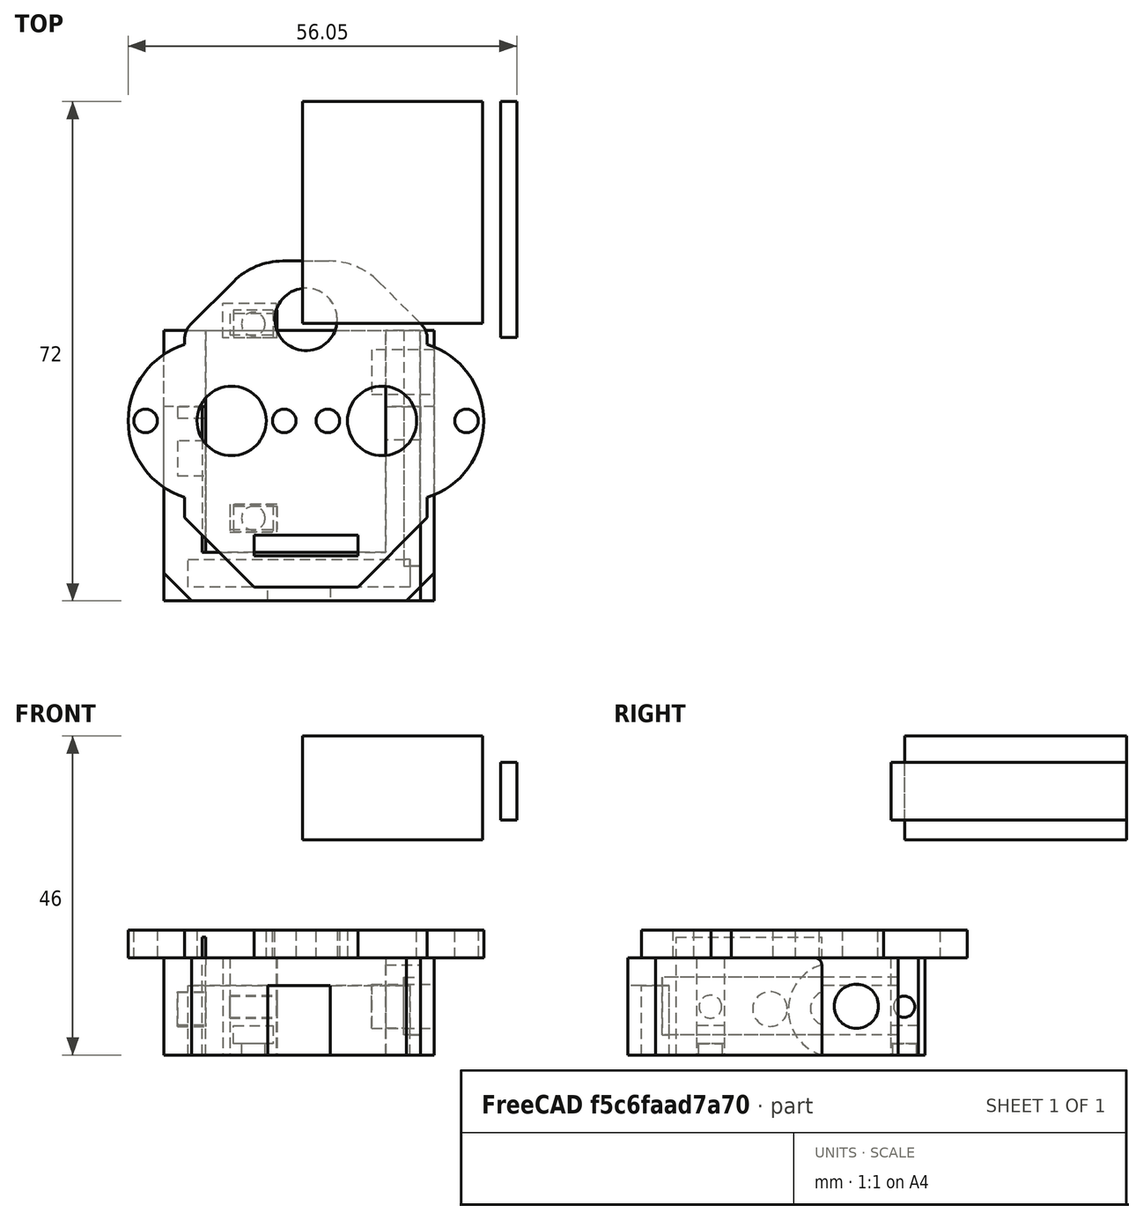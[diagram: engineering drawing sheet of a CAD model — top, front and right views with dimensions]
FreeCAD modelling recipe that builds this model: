
FCSTD DOCUMENT  (FreeCAD 0.14R2935 (Git))
Label: cuello3
License: CC-BY 3.0
LicenseURL: http://creativecommons.org/licenses/by/3.0/
objects: Sketcher::SketchObject×9, PartDesign::Pocket×8, Part::Feature×3, Part::Box×3, PartDesign::Fillet×3, PartDesign::Chamfer×2, Mesh::Feature×1, PartDesign::Pad×1, Part::MultiFuse×1, Part::Cut×1
note: 40 computed .brp shape members not serialized (recipe doc carries the construction recipe); baked Part::Feature solids carry a one-line shape summary decoded from their .brp

FEATURE [Part::Feature] Pad  label="Pad008"
  shape: bbox 51.29 x 47 x 18 mm, 56 faces (baked)
FEATURE [Mesh::Feature] _g_servo  label="9g_servo"
  Placement = pos=(3,-10,-24) rot=(0.57735,0.57735,0.57735;2.0944rad)
FEATURE [Part::Box] Box
  Height = 14
  Length = 37
  Placement = pos=(-14,-33,-31) rot=(0,0,1;0rad)
  Width = 39
FEATURE [Sketcher::SketchObject] Sketch
  ExternalGeometry = -> [Box]
  Placement = pos=(-14,-33,-31) rot=(1,0,0;3.14159rad)
  Support = -> Box [Face5]
  sketch-geometry (4):
    g0: LineSegment StartX=32 StartY=-39 StartZ=0 EndX=6 EndY=-39 EndZ=0
    g1: LineSegment StartX=6 StartY=-39 StartZ=0 EndX=6 EndY=-7 EndZ=0
    g2: LineSegment StartX=6 StartY=-7 StartZ=0 EndX=32 EndY=-7 EndZ=0
    g3: LineSegment StartX=32 StartY=-7 StartZ=0 EndX=32 EndY=-39 EndZ=0
  constraints (12):
    c: Coincident(g0,g1)
    c: Coincident(g1,g2)
    c: Coincident(g2,g3)
    c: Coincident(g3,g0)
    c: Horizontal(g0)
    c: Horizontal(g2)
    c: Vertical(g1)
    c: Vertical(g3)
    c: PointOnObject(g0,g-3)
    c: DistanceX(g-2,g1) = 6
    c: Distance(g2,g-4) = 5
    c: DistanceY(g-1,g2) = -7
FEATURE [PartDesign::Pocket] Pocket
  Length = 15
  Placement = pos=(-14,-33,-31) rot=(0,0,1;0rad)
  Sketch = -> Sketch
  Type = 0
FEATURE [Sketcher::SketchObject] Sketch001
  ExternalGeometry = -> [Pocket]
  Placement = pos=(-14,6,-31) rot=(0,0.707107,0.707107;3.14159rad)
  Support = -> Pocket [Face10]
  sketch-geometry (4):
    g0: LineSegment StartX=-36.9 StartY=11.215 StartZ=0 EndX=-34.6 EndY=11.215 EndZ=0
    g1: LineSegment StartX=-34.6 StartY=11.215 StartZ=0 EndX=-34.6 EndY=2.91495 EndZ=0
    g2: LineSegment StartX=-34.6 StartY=2.91495 StartZ=0 EndX=-36.9 EndY=2.91495 EndZ=0
    g3: LineSegment StartX=-36.9 StartY=2.91495 StartZ=0 EndX=-36.9 EndY=11.215 EndZ=0
  constraints (11):
    c: Coincident(g0,g1)
    c: Coincident(g1,g2)
    c: Coincident(g2,g3)
    c: Coincident(g3,g0)
    c: Horizontal(g0)
    c: Horizontal(g2)
    c: Vertical(g1)
    c: Vertical(g3)
    c: DistanceX(g2) = -2.3
    c: DistanceY(g3) = 8.3
    c: Distance(g0,g-3) = 2.6
FEATURE [PartDesign::Pocket] Pocket001
  Length = 34
  Placement = pos=(-14,-33,-31) rot=(0,0,1;0rad)
  Sketch = -> Sketch001
  Type = 0
FEATURE [Sketcher::SketchObject] Sketch002
  ExternalGeometry = -> [Pocket001]
  Placement = pos=(23,-33,-31) rot=(0.57735,0.57735,0.57735;2.0944rad)
  Support = -> Pocket001 [Face6]
  sketch-geometry (4):
    g0: LineSegment StartX=0 StartY=14 StartZ=0 EndX=39 EndY=14 EndZ=0
    g1: LineSegment StartX=39 StartY=14 StartZ=0 EndX=39 EndY=0 EndZ=0
    g2: LineSegment StartX=39 StartY=0 StartZ=0 EndX=0 EndY=0 EndZ=0
    g3: LineSegment StartX=0 StartY=0 StartZ=0 EndX=0 EndY=14 EndZ=0
  constraints (11):
    c: Coincident(g0,g1)
    c: Coincident(g1,g2)
    c: Coincident(g2,g3)
    c: Coincident(g3,g0)
    c: Horizontal(g0)
    c: Horizontal(g2)
    c: Vertical(g1)
    c: Vertical(g3)
    c: Coincident(g1,g-4)
    c: Coincident(g0,g-4)
    c: Coincident(g0,g-3)
FEATURE [PartDesign::Pad] Pad001
  Length = 2
  Length2 = 100
  Placement = pos=(-14,-33,-31) rot=(0,0,1;0rad)
  Sketch = -> Sketch002
  Type = 0
FEATURE [Part::Feature] Pad002  label="Pad009"
  shape: bbox 39 x 39 x 14 mm, 15 faces (baked)
FEATURE [Sketcher::SketchObject] Sketch003
  Placement = pos=(25,0,0) rot=(0.57735,0.57735,0.57735;2.0944rad)
  Support = -> Pad002 [Face1]
  sketch-geometry (1):
    g0: Circle CenterX=0 CenterY=-23.9671 CenterZ=0 NormalX=0 NormalY=0 NormalZ=1 Radius=3.18985
  constraints (1):
    c: PointOnObject(g0,g-2)
FEATURE [PartDesign::Pocket] Pocket002
  Length = 9
  Sketch = -> Sketch003
  Type = 0
FEATURE [Sketcher::SketchObject] Sketch004
  ExternalGeometry = -> [Pocket002]
  Placement = pos=(0,6,0) rot=(0,0.707107,0.707107;3.14159rad)
  Support = -> Pocket002 [Face4]
  sketch-geometry (4):
    g0: LineSegment StartX=-20.6 StartY=-21.0207 StartZ=0 EndX=-18 EndY=-21.0207 EndZ=0
    g1: LineSegment StartX=-18 StartY=-21.0207 StartZ=0 EndX=-18 EndY=-27.0975 EndZ=0
    g2: LineSegment StartX=-18 StartY=-27.0975 StartZ=0 EndX=-20.6 EndY=-27.0975 EndZ=0
    g3: LineSegment StartX=-20.6 StartY=-27.0975 StartZ=0 EndX=-20.6 EndY=-21.0207 EndZ=0
  constraints (10):
    c: Coincident(g0,g1)
    c: Coincident(g1,g2)
    c: Coincident(g2,g3)
    c: Coincident(g3,g0)
    c: Horizontal(g0)
    c: Horizontal(g2)
    c: Vertical(g1)
    c: Vertical(g3)
    c: PointOnObject(g2,g-4)
    c: PointOnObject(g1,g-3)
FEATURE [PartDesign::Pocket] Pocket003
  Length = 11
  Sketch = -> Sketch004
  Type = 0
FEATURE [Sketcher::SketchObject] Sketch005
  Placement = pos=(-8,0,0) rot=(0.57735,0.57735,0.57735;2.0944rad)
  Support = -> Pocket003 [Face11]
  sketch-geometry (1):
    g0: Circle CenterX=-12.4674 CenterY=-24.377 CenterZ=0 NormalX=0 NormalY=0 NormalZ=1 Radius=2.5
  constraints (1):
    c: Radius(g0) = 2.5
FEATURE [PartDesign::Pocket] Pocket004
  Length = 4
  Sketch = -> Sketch005
  Type = 0
FEATURE [Sketcher::SketchObject] Sketch006
  ExternalGeometry = -> [Pocket004]
  Placement = pos=(0,0,-31) rot=(1,0,0;3.14159rad)
  Support = -> Pocket004 [Face5]
  sketch-geometry (10):
    g0: LineSegment StartX=1 StartY=31 StartZ=0 EndX=-10.5 EndY=31 EndZ=0
    g1: LineSegment StartX=-10.5 StartY=31 StartZ=0 EndX=-10.5 EndY=27 EndZ=0
    g2: LineSegment StartX=-10.5 StartY=27 StartZ=0 EndX=21.5 EndY=27 EndZ=0
    g3: LineSegment StartX=21.5 StartY=27 StartZ=0 EndX=21.5 EndY=31 EndZ=0
    g4: LineSegment StartX=21.5 StartY=31 StartZ=0 EndX=10 EndY=31 EndZ=0
    g5: LineSegment StartX=10 StartY=31 StartZ=0 EndX=10 EndY=33 EndZ=0
    g6: LineSegment StartX=10 StartY=33 StartZ=0 EndX=1 EndY=33 EndZ=0
    g7: LineSegment StartX=1 StartY=33 StartZ=0 EndX=1 EndY=31 EndZ=0
    g8: LineSegment [constr] StartX=-14 StartY=31 StartZ=0 EndX=-10.5 EndY=31 EndZ=0
    g9: LineSegment [constr] StartX=21.5 StartY=31 StartZ=0 EndX=25 EndY=31 EndZ=0
  constraints (30):
    c: Horizontal(g0)
    c: Coincident(g0,g1)
    c: Coincident(g1,g2)
    c: Horizontal(g2)
    c: Coincident(g2,g3)
    c: Coincident(g3,g4)
    c: Horizontal(g4)
    c: Coincident(g4,g5)
    c: Coincident(g5,g6)
    c: Horizontal(g6)
    c: Coincident(g6,g7)
    c: Vertical(g7)
    c: Vertical(g5)
    c: Coincident(g7,g0)
    c: PointOnObject(g6,g-3)
    c: Vertical(g3)
    c: DistanceY(g3) = 4
    c: DistanceX(g6,g5) = 9
    c: Equal(g0,g4)
    c: DistanceX(g2) = 32
    c: Vertical(g1)
    c: DistanceY(g7) = -2
    c: Equal(g7,g5)
    c: Horizontal(g8)
    c: Horizontal(g9)
    c: Equal(g8,g9)
    c: PointOnObject(g8,g-4)
    c: PointOnObject(g9,g-5)
    c: Coincident(g9,g3)
    c: Coincident(g8,g0)
FEATURE [PartDesign::Pocket] Pocket005
  Length = 10
  Sketch = -> Sketch006
  Type = 0
FEATURE [PartDesign::Fillet] Fillet
  Base = -> Pocket005 [Edge44]
  Radius = 5
FEATURE [PartDesign::Chamfer] Chamfer
  Base = -> Fillet [Edge18]
  Size = 4
FEATURE [PartDesign::Chamfer] Chamfer001
  Base = -> Chamfer [Edge21]
  Size = 4
FEATURE [Part::Box] Box001
  Height = 16
  Length = 11
  Placement = pos=(16,-5,-32) rot=(0,0,1;0rad)
  Width = 12
FEATURE [Part::Box] Box002
  Height = 16
  Length = 11
  Placement = pos=(-16,-5,-32) rot=(0,0,1;0rad)
  Width = 12
FEATURE [Part::MultiFuse] Fusion
  Shapes = -> [Box002,Box001]
FEATURE [Part::Cut] Cut
  Base = -> Chamfer001
  Tool = -> Fusion
FEATURE [PartDesign::Fillet] Fillet001
  Base = -> Cut [Edge8]
  Radius = 1
FEATURE [PartDesign::Fillet] Fillet002
  Base = -> Fillet001 [Edge7]
  Radius = 1
FEATURE [Part::Feature] Fillet003
  shape: bbox 39 x 28 x 14 mm, 29 faces (baked)
FEATURE [Sketcher::SketchObject] Sketch007
  ExternalGeometry = -> [Fillet003]
  Placement = pos=(18,0,0) rot=(0.57735,-0.57735,-0.57735;2.0944rad)
  Support = -> Fillet003 [Face6]
  sketch-geometry (2):
    g0: ArcOfCircle CenterX=3.04673 CenterY=-24.5 CenterZ=0 NormalX=0 NormalY=0 NormalZ=1 Radius=6.78714 StartAngle=5.00431 EndAngle=7.56206
    g1: LineSegment StartX=5 StartY=-18 StartZ=0 EndX=5 EndY=-31 EndZ=0
  constraints (6):
    c: Coincident(g0,g-3)
    c: Coincident(g0,g-3)
    c: Vertical(g1)
    c: Coincident(g1,g0)
    c: Coincident(g1,g0)
    c: Radius(g0) = 6.78714
FEATURE [PartDesign::Pocket] Pocket006
  Length = 5
  Sketch = -> Sketch007
  Type = 0
FEATURE [Sketcher::SketchObject] Sketch008
  ExternalGeometry = -> [Pocket006]
  Placement = pos=(0,0,-31) rot=(1,0,0;3.14159rad)
  Support = -> Pocket006 [Face13]
  sketch-geometry (4):
    g0: LineSegment StartX=-8.5 StartY=26 StartZ=0 EndX=-8 EndY=26 EndZ=0
    g1: LineSegment StartX=-8 StartY=26 StartZ=0 EndX=-8 EndY=5 EndZ=0
    g2: LineSegment StartX=-8 StartY=5 StartZ=0 EndX=-8.5 EndY=5 EndZ=0
    g3: LineSegment StartX=-8.5 StartY=5 StartZ=0 EndX=-8.5 EndY=26 EndZ=0
  constraints (11):
    c: Coincident(g0,g1)
    c: Coincident(g1,g2)
    c: Coincident(g2,g3)
    c: Coincident(g3,g0)
    c: Horizontal(g0)
    c: Horizontal(g2)
    c: Vertical(g1)
    c: Vertical(g3)
    c: DistanceX(g0) = 0.5
    c: Coincident(g0,g-3)
    c: Coincident(g1,g-3)
FEATURE [PartDesign::Pocket] Pocket007
  Length = 17
  Sketch = -> Sketch008
  Type = 0
